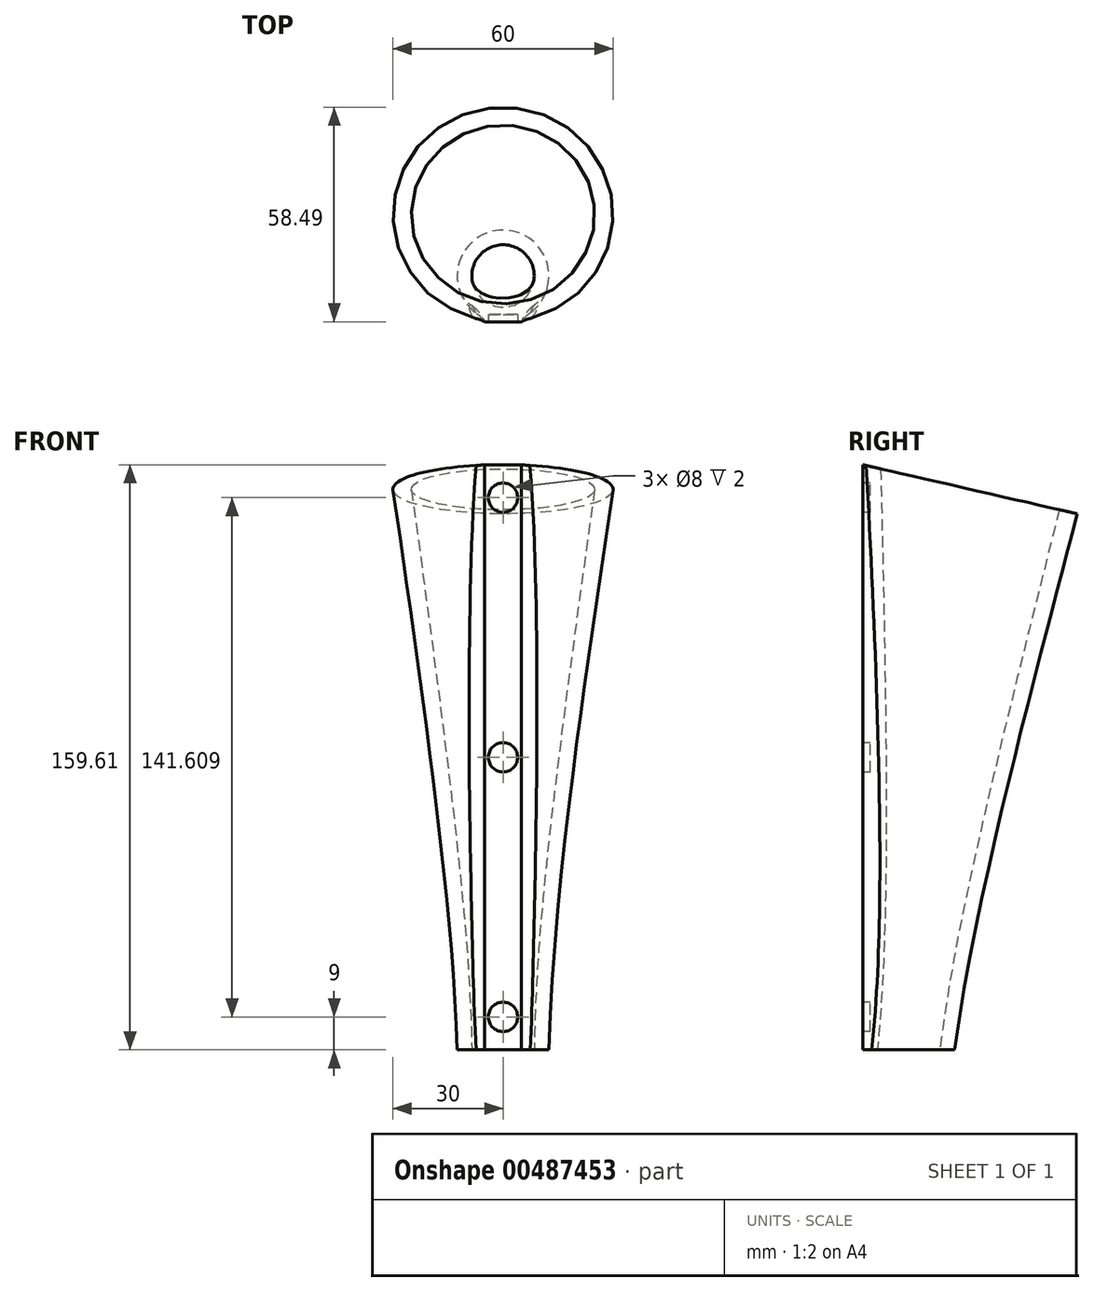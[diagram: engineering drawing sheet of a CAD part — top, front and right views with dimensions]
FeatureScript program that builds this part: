
annotation { "Feature Type Name" : "Feature", "Feature Type Description" : "" }
export const myFeature = defineFeature(function(context is Context, id is Id, definition is map)
    precondition{}
    {
        {
            var Q0;
            Q0=qCreatedBy(makeId("Right.planeOp"),FACE);
            var sketch = newSketch(context, id + "F0", { "sketchPlane" : qUnion([Q0])});
            skLineSegment(sketch, "E0", {"start": v(0, 0) * mm, "end": v(0, 159.6) * mm, "construction": true});
            skLineSegment(sketch, "E1", {"start": v(0, 159.6) * mm, "end": v(58.49, 146.21) * mm, "construction": true});
            skLineSegment(sketch, "E2", {"start": v(58.49, 146.21) * mm, "end": v(25, 0) * mm, "construction": true});
            skLineSegment(sketch, "E3", {"start": v(25, 0) * mm, "end": v(0, 0) * mm, "construction": true});
            skSolve(sketch);
        }
        {
            var Q0;
            Q0=sQuery(id+"F0.wireOp",EDGE,"E1");
            cPlane(context, id + "F1", {"entities" : qUnion([Q0]), "cplaneType" : CPlaneType.LINE_ANGLE, "offset" : 25 * mm, "angle" : 0 * degree, "width" : 150 * mm, "height" : 150 * mm});
        }
        {
            var Q0;
            Q0=qCreatedBy(id+"F1.planeOp",FACE);
            var sketch = newSketch(context, id + "F2", { "sketchPlane" : qUnion([Q0])});
            skLineSegment(sketch, "E4.0", {"start": v(0, -35.63) * mm, "end": v(0, 24.37) * mm, "construction": true});
            skCircle(sketch, "E5", {"center": v(0, -5.63) * mm, "radius": 30 * mm});
            skSolve(sketch);
        }
        {
            var Q0;
            Q0=sQuery(id+"F0.wireOp",EDGE,"E3");
            cPlane(context, id + "F3", {"entities" : qUnion([Q0]), "cplaneType" : CPlaneType.LINE_ANGLE, "offset" : 25 * mm, "angle" : 0 * degree, "width" : 150 * mm, "height" : 150 * mm});
        }
        {
            var Q0;
            Q0=qCreatedBy(id+"F3.planeOp",FACE);
            var sketch = newSketch(context, id + "F4", { "sketchPlane" : qUnion([Q0])});
            skLineSegment(sketch, "E6.0", {"start": v(0, -25) * mm, "end": v(0, 0) * mm, "construction": true});
            skCircle(sketch, "E7", {"center": v(0, -12.5) * mm, "radius": 12.5 * mm});
            skSolve(sketch);
        }
        {
            var Q0;
            Q0=qCreatedBy(makeId("Top.planeOp"),FACE);
            var sketch = newSketch(context, id + "F5", { "sketchPlane" : qUnion([Q0])});
            skLineSegment(sketch, "E8", {"start": v(-5, 0) * mm, "end": v(5, 0) * mm});
            skLineSegment(sketch, "E9", {"start": v(5, 0) * mm, "end": v(5, 2.2) * mm});
            skLineSegment(sketch, "E10", {"start": v(5, 2.2) * mm, "end": v(-5, 2.2) * mm});
            skLineSegment(sketch, "E11", {"start": v(-5, 2.2) * mm, "end": v(-5, 0) * mm});
            skSolve(sketch);
        }
        {
            var Q0;
            Q0=makeQuery(id+"F4.imprint","IMPRINT",FACE,{"disambiguationData":[TD([[makeQuery(id+"F4.imprint","IMPRINT",EDGE,{"derivedFrom":sQuery(id+"F4.wireOp",EDGE,"E7")}),1.0]])]});
            var Q1;
            Q1=makeQuery(id+"F2.imprint","IMPRINT",FACE,{"disambiguationData":[TD([[makeQuery(id+"F2.imprint","IMPRINT",EDGE,{"derivedFrom":sQuery(id+"F2.wireOp",EDGE,"E5")}),1.0]])]});
            loft(context, id + "F6", {"sheetProfilesArray" : [{ "sheetProfileEntities" : qUnion([Q0]) }, { "sheetProfileEntities" : qUnion([Q1]) }]});
        }
        {
            var Q0;
            Q0=makeQuery(id+"F6.opLoft","CAP_FACE",FACE,{"disambiguationData":[OSD([makeQuery(id+"F2.imprint","IMPRINT",FACE,{"disambiguationData":[TD([[makeQuery(id+"F2.imprint","IMPRINT",EDGE,{"derivedFrom":sQuery(id+"F2.wireOp",EDGE,"E5")}),1.0]])]})])],"isStart":true});
            var sketch = newSketch(context, id + "F7", { "sketchPlane" : qUnion([Q0])});
            skLineSegment(sketch, "E12.0", {"start": v(0, -35.63) * mm, "end": v(0, 24.37) * mm, "construction": true});
            skCircle(sketch, "E13", {"center": v(0, -5.63) * mm, "radius": 25 * mm});
            skLineSegment(sketch, "E14.0", {"start": v(0, 24.37) * mm, "end": v(0, 0) * mm, "construction": true});
            skLineSegment(sketch, "E15", {"start": v(0, 0) * mm, "end": v(0, 24.37) * mm});
            skSolve(sketch);
        }
        {
            var Q0;
            Q0=makeQuery(id+"F6.opLoft","CAP_FACE",FACE,{"disambiguationData":[OSD([makeQuery(id+"F4.imprint","IMPRINT",FACE,{"disambiguationData":[TD([[makeQuery(id+"F4.imprint","IMPRINT",EDGE,{"derivedFrom":sQuery(id+"F4.wireOp",EDGE,"E7")}),1.0]])]})])],"isStart":true});
            var sketch = newSketch(context, id + "F8", { "sketchPlane" : qUnion([Q0])});
            skFitSpline(sketch, "E16.0", {"points": [v(7.1, -4.56) * mm, v(7.7, -7.5) * mm, v(7.1, -10.44) * mm, v(5.44, -12.94) * mm, v(2.94, -14.6) * mm, v(0, -15.2) * mm, v(-2.94, -14.6) * mm, v(-5.44, -12.94) * mm, v(-7.1, -10.44) * mm, v(-7.7, -7.5) * mm, v(-7.1, -4.56) * mm, v(-5.44, -2.06) * mm, v(-2.94, -0.4) * mm, v(0, 0.2) * mm, v(2.94, -0.4) * mm, v(5.44, -2.06) * mm, v(7.1, -4.56) * mm, v(7.7, -7.5) * mm, v(7.1, -10.44) * mm, v(7.1, -4.56) * mm]});
            skLineSegment(sketch, "E17", {"start": v(0, 0) * mm, "end": v(0, -25) * mm, "construction": true});
            skCircle(sketch, "E18", {"center": v(0, -12.5) * mm, "radius": 8.5 * mm});
            skSolve(sketch);
        }
        {
            var Q1;
            Q1=makeQuery(id+"F8.imprint","IMPRINT",FACE,{"disambiguationData":[TD([[makeQuery(id+"F8.imprint","IMPRINT",EDGE,{"derivedFrom":sQuery(id+"F8.wireOp",EDGE,"E18")}),1.0]])]});
            var Q2;
            Q2=makeQuery(id+"F7.imprint","IMPRINT",FACE,{"disambiguationData":[TD([[makeQuery(id+"F7.imprint","IMPRINT",EDGE,{"derivedFrom":sQuery(id+"F7.wireOp",EDGE,"E13")}),1.0]])]});
            loft(context, id + "F9", {"operationType" : NewBodyOperationType.REMOVE, "sheetProfilesArray" : [{ "sheetProfileEntities" : qUnion([Q1]) }, { "sheetProfileEntities" : qUnion([Q2]) }]});
        }
        {
            var Q0;
            Q0=makeQuery(id+"F5.imprint","IMPRINT",FACE,{"disambiguationData":[TD([[makeQuery(id+"F5.imprint","IMPRINT",EDGE,{"derivedFrom":sQuery(id+"F5.wireOp",EDGE,"E8")}),1.0]])]});
            var Q1;
            Q1=qCreatedBy(id+"F1.planeOp",FACE);
            extrude(context, id + "F10", {"entities" : qUnion([Q0]), "operationType" : NewBodyOperationType.ADD, "endBound" : BoundingType.UP_TO_SURFACE, "endBoundEntityFace" : qUnion([Q1]), "depth" : 25 * mm});
        }
        {
            var Q0;
            Q0=makeQuery(id+"F10.boolean.opBoolean","MERGE",FACE,{"derivedFrom":[makeQuery(id+"F6.opLoft","CAP_FACE",FACE,{"disambiguationData":[OSD([makeQuery(id+"F4.imprint","IMPRINT",FACE,{"disambiguationData":[TD([[makeQuery(id+"F4.imprint","IMPRINT",EDGE,{"derivedFrom":sQuery(id+"F4.wireOp",EDGE,"E7")}),1.0]])]})])],"isStart":true}),makeQuery(id+"F10.opExtrude","CAP_FACE",FACE,{"disambiguationData":[OSD([sQuery(id+"F5.wireOp",EDGE,"E8"),sQuery(id+"F5.wireOp",EDGE,"E9"),sQuery(id+"F5.wireOp",EDGE,"E10"),sQuery(id+"F5.wireOp",EDGE,"E11")])],"isStart":true})]});
            var sketch = newSketch(context, id + "F11", { "sketchPlane" : qUnion([Q0])});
            skFitSpline(sketch, "E19.0", {"points": [v(5, -1.9) * mm, v(5.56, -2.41) * mm, v(6.53, -3.59) * mm, v(7.4, -5.7) * mm, v(7.6, -7.98) * mm, v(7.11, -10.22) * mm, v(5.99, -12.2) * mm, v(4.32, -13.77) * mm, v(2.26, -14.77) * mm, v(0, -15.11) * mm, v(-2.26, -14.77) * mm, v(-4.32, -13.77) * mm, v(-5.99, -12.2) * mm, v(-7.11, -10.22) * mm, v(-7.6, -7.98) * mm, v(-7.4, -5.7) * mm, v(-6.53, -3.59) * mm, v(-5.56, -2.41) * mm, v(-5, -1.9) * mm]});
            skLineSegment(sketch, "E20", {"start": v(0.1, -1.9) * mm, "end": v(-10.22, -5.3) * mm});
            skLineSegment(sketch, "E21", {"start": v(0.1, -1.9) * mm, "end": v(10.13, -5.17) * mm});
            skLineSegment(sketch, "E22", {"start": v(0.1, -1.9) * mm, "end": v(0, 0) * mm, "construction": true});
            skSolve(sketch);
        }
        {
            var Q0;
            Q0=makeQuery(id+"F10.opExtrude","SWEPT_FACE",FACE,{"disambiguationData":[OSD([sQuery(id+"F5.wireOp",EDGE,"E8")])]});
            var sketch = newSketch(context, id + "F12", { "sketchPlane" : qUnion([Q0])});
            skLineSegment(sketch, "E23.0", {"start": v(-5, 0) * mm, "end": v(5, 0) * mm});
            skLineSegment(sketch, "E23.1", {"start": v(-5, 159.6) * mm, "end": v(5, 159.6) * mm});
            skLineSegment(sketch, "E24", {"start": v(0, 0) * mm, "end": v(0, 159.6) * mm, "construction": true});
            skLineSegment(sketch, "E25", {"start": v(0, 79.8) * mm, "end": v(-5, 79.8) * mm, "construction": true});
            skCircle(sketch, "E26", {"center": v(0, 79.8) * mm, "radius": 4 * mm});
            skCircle(sketch, "E27", {"center": v(0, 9) * mm, "radius": 4 * mm});
            skCircle(sketch, "E28", {"center": v(0, 150.6) * mm, "radius": 4 * mm});
            skSolve(sketch);
        }
        {
            var Q0;
            Q0=makeQuery(id+"F12.imprint","IMPRINT",FACE,{"disambiguationData":[TD([[makeQuery(id+"F12.imprint","IMPRINT",EDGE,{"derivedFrom":sQuery(id+"F12.wireOp",EDGE,"E27")}),1.0]])]});
            var Q1;
            Q1=makeQuery(id+"F12.imprint","IMPRINT",FACE,{"disambiguationData":[TD([[makeQuery(id+"F12.imprint","IMPRINT",EDGE,{"derivedFrom":sQuery(id+"F12.wireOp",EDGE,"E26")}),1.0]])]});
            var Q2;
            Q2=makeQuery(id+"F12.imprint","IMPRINT",FACE,{"disambiguationData":[TD([[makeQuery(id+"F12.imprint","IMPRINT",EDGE,{"derivedFrom":sQuery(id+"F12.wireOp",EDGE,"E28")}),1.0]])]});
            extrude(context, id + "F13", {"entities" : qUnion([Q0, Q1, Q2]), "operationType" : NewBodyOperationType.REMOVE, "oppositeDirection" : true, "depth" : 2 * mm});
        }
        {
            var Q0;
            Q0=makeQuery(id+"F10.opExtrude","SWEPT_EDGE",EDGE,{"disambiguationData":[OSD([sQuery(id+"F5.wireOp",EDGE,"E9"),sQuery(id+"F5.wireOp",EDGE,"E10")])]});
            var Q1;
            Q1=makeQuery(id+"F10.boolean.opBoolean","INTERSECT",EDGE,{"disambiguationData":[OD(0.0)],"derivedFrom":[makeQuery(id+"F6.opLoft","SWEPT_FACE",FACE,{"disambiguationData":[OSD([sQuery(id+"F2.wireOp",EDGE,"E5"),sQuery(id+"F4.wireOp",EDGE,"E7")])]}),makeQuery(id+"F10.opExtrude","SWEPT_FACE",FACE,{"disambiguationData":[OSD([sQuery(id+"F5.wireOp",EDGE,"E9")])]})]});
            fillet(context, id + "F14", {"entities" : qUnion([Q0, Q1]), "radius" : 10 * mm, "tangentPropagation" : true, "allowEdgeOverflow" : false});
        }
        {
            var Q0;
            Q0=makeQuery(id+"F10.opExtrude","SWEPT_EDGE",EDGE,{"disambiguationData":[OSD([sQuery(id+"F5.wireOp",EDGE,"E10"),sQuery(id+"F5.wireOp",EDGE,"E11")])]});
            var Q1;
            Q1=makeQuery(id+"F10.boolean.opBoolean","INTERSECT",EDGE,{"disambiguationData":[OD(0.0)],"derivedFrom":[makeQuery(id+"F6.opLoft","SWEPT_FACE",FACE,{"disambiguationData":[OSD([sQuery(id+"F2.wireOp",EDGE,"E5"),sQuery(id+"F4.wireOp",EDGE,"E7")])]}),makeQuery(id+"F10.opExtrude","SWEPT_FACE",FACE,{"disambiguationData":[OSD([sQuery(id+"F5.wireOp",EDGE,"E11")])]})]});
            fillet(context, id + "F15", {"entities" : qUnion([Q0, Q1]), "radius" : 10 * mm, "tangentPropagation" : true, "allowEdgeOverflow" : false});
        }
    });
